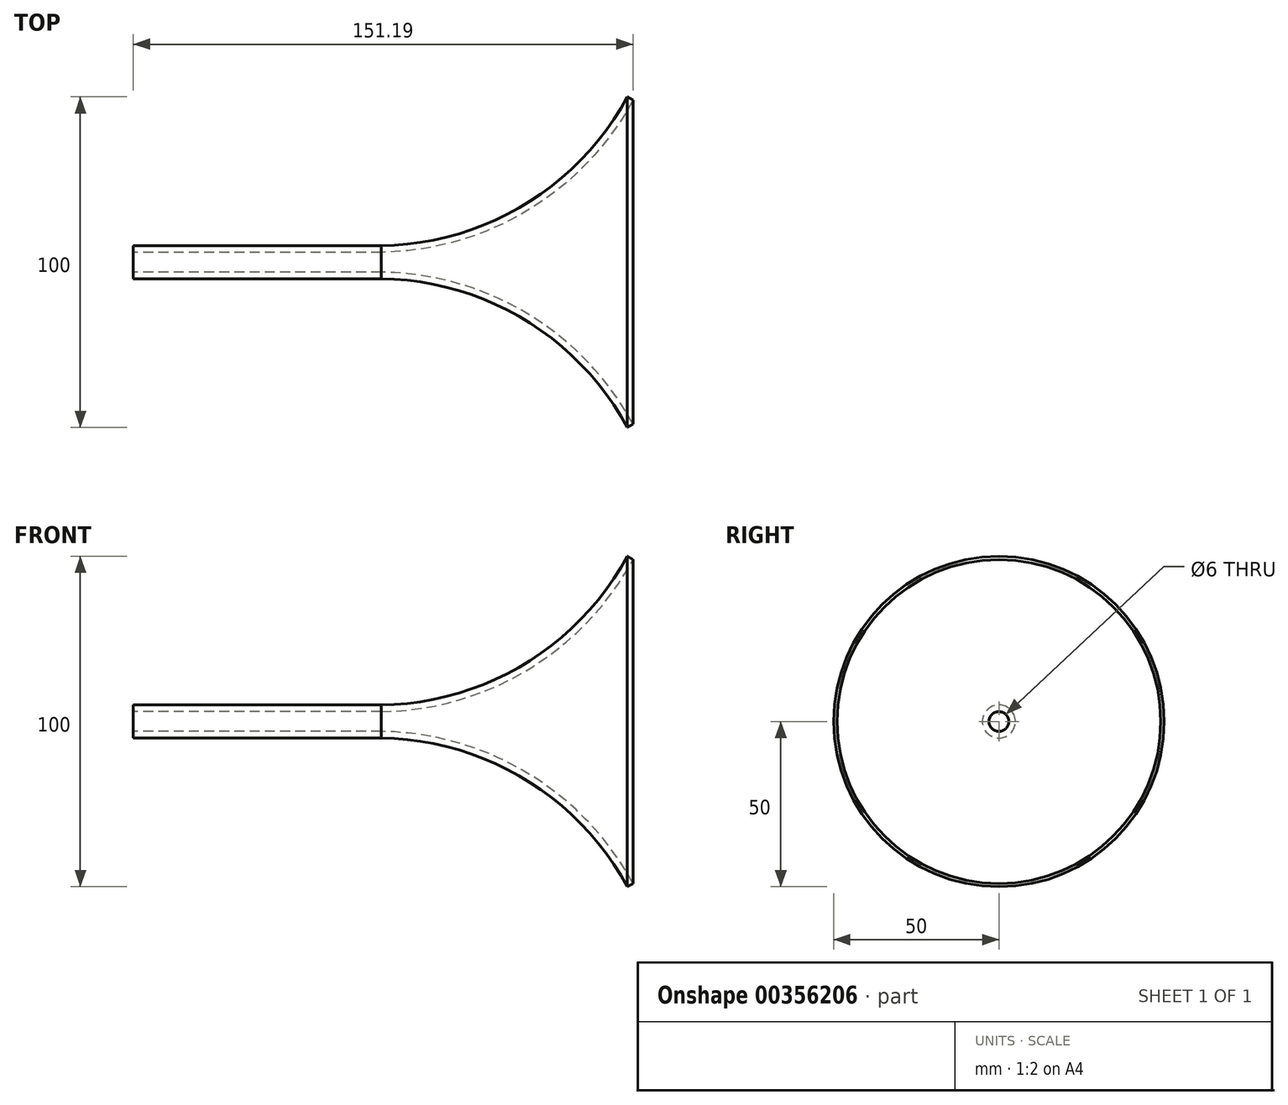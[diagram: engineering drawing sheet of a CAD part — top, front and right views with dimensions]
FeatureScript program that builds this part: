
annotation { "Feature Type Name" : "Feature", "Feature Type Description" : "" }
export const myFeature = defineFeature(function(context is Context, id is Id, definition is map)
    precondition{}
    {
        {
            var Q0;
            Q0=qCreatedBy(makeId("Top.planeOp"),FACE);
            var sketch = newSketch(context, id + "F0", { "sketchPlane" : qUnion([Q0])});
            skPoint(sketch, "E0.orphan", {"position": v(76.47, 0) * mm});
            skLineSegment(sketch, "E1", {"start": v(-75, 5) * mm, "end": v(0, 5) * mm});
            skArc(sketch, "E2", {"start": v(0, 5) * mm, "mid": v(43.34, 17.4) * mm, "end": v(74.46, 50) * mm});
            skLineSegment(sketch, "E3", {"start": v(-74.1, 0) * mm, "end": v(63.88, 0) * mm, "construction": true});
            skPoint(sketch, "E3.endSnap0", {"position": v(-75, 0) * mm});
            skPoint(sketch, "E4.start.orphan", {"position": v(0, -5) * mm});
            skPoint(sketch, "E5.orphan", {"position": v(-75, -5) * mm});
            skPoint(sketch, "E6.start.orphan", {"position": v(75, -50) * mm});
            skArc(sketch, "E7.0", {"start": v(0.01, 3) * mm, "mid": v(44.35, 15.66) * mm, "end": v(76.2, 49) * mm});
            skLineSegment(sketch, "E7.1", {"start": v(-75, 3) * mm, "end": v(0.01, 3) * mm});
            skLineSegment(sketch, "E8", {"start": v(76.2, 49) * mm, "end": v(74.46, 50) * mm});
            skLineSegment(sketch, "E9", {"start": v(-75, 3) * mm, "end": v(-75, 5) * mm});
            skSolve(sketch);
        }
        {
            var Q0;
            Q0=makeQuery(id+"F0.imprint","IMPRINT",FACE,{"disambiguationData":[TD([[makeQuery(id+"F0.imprint","IMPRINT",EDGE,{"derivedFrom":sQuery(id+"F0.wireOp",EDGE,"E1")}),-1.0]])]});
            var Q1;
            Q1=sQuery(id+"F0.wireOp",EDGE,"E1");
            var Q2;
            Q2=sQuery(id+"F0.wireOp",EDGE,"E2");
            var Q3;
            Q3=sQuery(id+"F0.wireOp",EDGE,"TP0Xv1eM-mswl-S0iQ-tXDp-io6CKMhfxeet");
            var Q4;
            Q4=sQuery(id+"F0.wireOp",EDGE,"E3");
            revolve(context, id + "F1", {"entities" : qUnion([Q0]), "surfaceEntities" : qUnion([Q1, Q2, Q3]), "axis" : qUnion([Q4]), "revolveType" : RevolveType.FULL});
        }
    });
